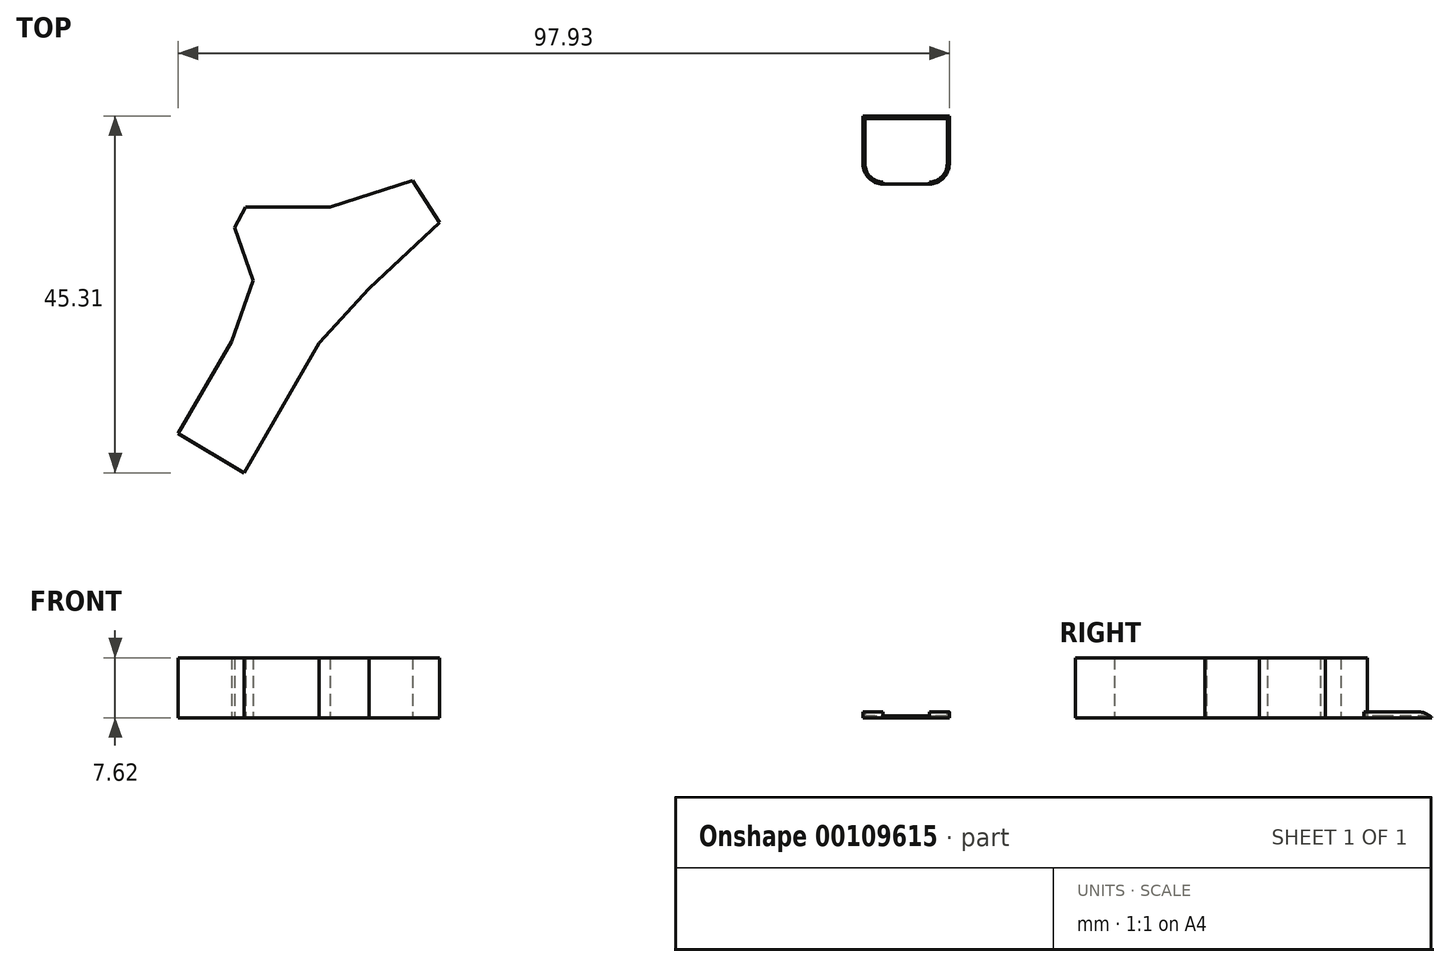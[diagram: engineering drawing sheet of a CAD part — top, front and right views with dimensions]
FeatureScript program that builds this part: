
annotation { "Feature Type Name" : "Feature", "Feature Type Description" : "" }
export const myFeature = defineFeature(function(context is Context, id is Id, definition is map)
    precondition{}
    {
        {
            var Q0;
            Q0=qCreatedBy(makeId("Top.planeOp"),FACE);
            var sketch = newSketch(context, id + "F0", { "sketchPlane" : qUnion([Q0])});
            skLineSegment(sketch, "E0", {"start": v(-24.22, -6.35) * mm, "end": v(-17.47, 5.36) * mm});
            skLineSegment(sketch, "E1", {"start": v(-17.47, 5.36) * mm, "end": v(-14.7, 13.1) * mm});
            skLineSegment(sketch, "E2", {"start": v(-14.7, 13.1) * mm, "end": v(-17.07, 19.85) * mm});
            skLineSegment(sketch, "E3", {"start": v(-17.07, 19.85) * mm, "end": v(-15.68, 22.43) * mm});
            skLineSegment(sketch, "E4", {"start": v(-15.68, 22.43) * mm, "end": v(-4.96, 22.43) * mm});
            skLineSegment(sketch, "E5", {"start": v(-4.96, 22.43) * mm, "end": v(5.56, 25.8) * mm});
            skLineSegment(sketch, "E6", {"start": v(5.56, 25.8) * mm, "end": v(8.93, 20.45) * mm});
            skLineSegment(sketch, "E7", {"start": v(8.93, 20.45) * mm, "end": v(0, 12.11) * mm});
            skLineSegment(sketch, "E8", {"start": v(0, 12.11) * mm, "end": v(-6.35, 5.16) * mm});
            skLineSegment(sketch, "E9", {"start": v(-6.35, 5.16) * mm, "end": v(-15.88, -11.32) * mm});
            skLineSegment(sketch, "E10", {"start": v(-15.88, -11.32) * mm, "end": v(-24.22, -6.35) * mm});
            skSolve(sketch);
        }
        {
            var Q0;
            Q0=makeQuery(id+"F0.imprint","IMPRINT",FACE,{"disambiguationData":[TD([[makeQuery(id+"F0.imprint","IMPRINT",EDGE,{"derivedFrom":sQuery(id+"F0.wireOp",EDGE,"E0")}),-1.0]])]});
            extrude(context, id + "F1", {"entities" : qUnion([Q0]), "depth" : 7.62 * mm});
        }
        {
            var Q0;
            Q0=qCreatedBy(makeId("Top.planeOp"),FACE);
            var sketch = newSketch(context, id + "F2", { "sketchPlane" : qUnion([Q0])});
            skLineSegment(sketch, "E11", {"start": v(62.76, 34) * mm, "end": v(62.76, 27.92) * mm});
            skLineSegment(sketch, "E12", {"start": v(65.3, 25.38) * mm, "end": v(71.17, 25.38) * mm});
            skLineSegment(sketch, "E13", {"start": v(73.7, 27.92) * mm, "end": v(73.7, 34) * mm});
            skLineSegment(sketch, "E14", {"start": v(73.7, 34) * mm, "end": v(62.76, 34) * mm});
            skPoint(sketch, "E15.visualSharp", {"position": v(62.76, 25.38) * mm});
            skArc(sketch, "E15.filletArc", {"start": v(62.76, 27.92) * mm, "mid": v(63.5, 26.12) * mm, "end": v(65.3, 25.38) * mm});
            skPoint(sketch, "E16.visualSharp", {"position": v(73.7, 25.38) * mm});
            skArc(sketch, "E16.filletArc", {"start": v(71.17, 25.38) * mm, "mid": v(72.97, 26.12) * mm, "end": v(73.7, 27.92) * mm});
            skSolve(sketch);
        }
        {
            var Q0;
            Q0=makeQuery(id+"F2.imprint","IMPRINT",FACE,{"disambiguationData":[TD([[makeQuery(id+"F2.imprint","IMPRINT",EDGE,{"derivedFrom":sQuery(id+"F2.wireOp",EDGE,"E11")}),1.0]])]});
            extrude(context, id + "F3", {"entities" : qUnion([Q0]), "depth" : 0.76 * mm});
        }
        {
            var Q0;
            Q0=makeQuery(id+"F3.opExtrude","CAP_FACE",FACE,{"disambiguationData":[OSD([sQuery(id+"F2.wireOp",EDGE,"E11"),sQuery(id+"F2.wireOp",EDGE,"E12"),sQuery(id+"F2.wireOp",EDGE,"E13"),sQuery(id+"F2.wireOp",EDGE,"E14"),sQuery(id+"F2.wireOp",EDGE,"E15.filletArc"),sQuery(id+"F2.wireOp",EDGE,"E16.filletArc")])],"isStart":false});
            var Q1;
            Q1=makeQuery(id+"F3.opExtrude","SWEPT_FACE",FACE,{"disambiguationData":[OSD([sQuery(id+"F2.wireOp",EDGE,"E12")])]});
            var Q2;
            Q2=makeQuery(id+"F3.opExtrude","SWEPT_FACE",FACE,{"disambiguationData":[OSD([sQuery(id+"F2.wireOp",EDGE,"E14")])]});
            shell(context, id + "F4", {"entities" : qUnion([Q0, Q1, Q2]), "thickness" : 0.25 * mm});
        }
        {
            var Q0;
            Q0=makeQuery(id+"F3.opExtrude","CAP_EDGE",EDGE,{"disambiguationData":[OSD([sQuery(id+"F2.wireOp",EDGE,"E14")])],"isStart":false});
            var Q1;
            {var subQ0=sQuery(id+"F2.wireOp",EDGE,"E14");Q1=makeQuery(id+"F4.opShell","OFFSET_EDGE",EDGE,{"disambiguationData":[OSD([subQ0]),TDD([makeQuery(id+"F3.opExtrude","CAP_EDGE",EDGE,{"disambiguationData":[OSD([subQ0])],"isStart":false})])]});}
            fillet(context, id + "F5", {"entities" : qUnion([Q0, Q1]), "radius" : 2.54 * mm, "tangentPropagation" : true, "allowEdgeOverflow" : false});
        }
    });
